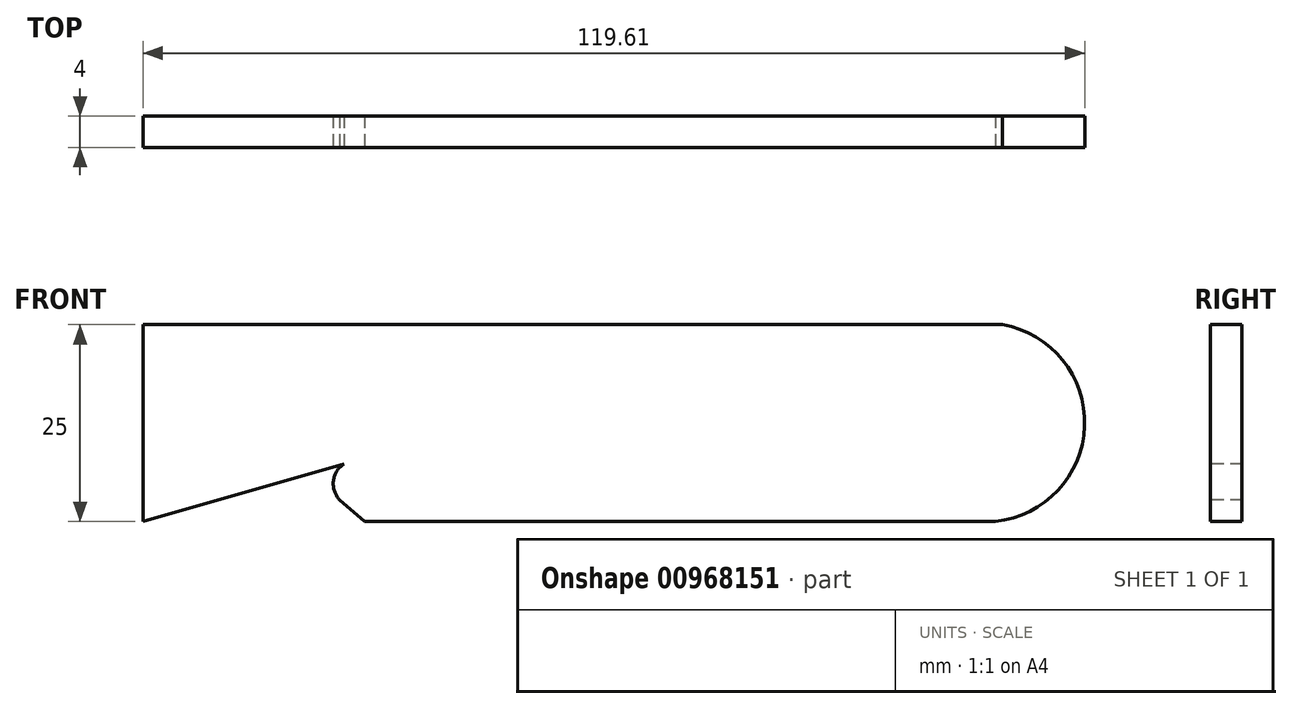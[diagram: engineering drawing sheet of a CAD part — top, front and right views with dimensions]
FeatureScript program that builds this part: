
annotation { "Feature Type Name" : "Feature", "Feature Type Description" : "" }
export const myFeature = defineFeature(function(context is Context, id is Id, definition is map)
    precondition{}
    {
        {
            var Q0;
            Q0=qCreatedBy(makeId("Front.planeOp"),FACE);
            var sketch = newSketch(context, id + "F0", { "sketchPlane" : qUnion([Q0])});
            skLineSegment(sketch, "E0.bottom", {"start": v(-16.89, -4.8) * mm, "end": v(103.11, -4.8) * mm});
            skLineSegment(sketch, "E0.top", {"start": v(-16.89, 20.2) * mm, "end": v(103.11, 20.2) * mm});
            skLineSegment(sketch, "E0.left", {"start": v(-16.89, -4.8) * mm, "end": v(-16.89, 20.2) * mm});
            skLineSegment(sketch, "E0.right", {"start": v(103.11, -4.8) * mm, "end": v(103.11, 20.2) * mm});
            skSolve(sketch);
        }
        {
            var Q0;
            Q0=makeQuery(id+"F0.imprint","IMPRINT",FACE,{"disambiguationData":[TD([[makeQuery(id+"F0.imprint","IMPRINT",EDGE,{"derivedFrom":sQuery(id+"F0.wireOp",EDGE,"E0.bottom")}),1.0]])]});
            extrude(context, id + "F1", {"entities" : qUnion([Q0]), "depth" : 4 * mm, "offsetDistance" : 25 * mm});
        }
        {
            var Q0;
            Q0=makeQuery(id+"F1.opExtrude","CAP_FACE",FACE,{"disambiguationData":[OSD([sQuery(id+"F0.wireOp",EDGE,"E0.bottom"),sQuery(id+"F0.wireOp",EDGE,"E0.top"),sQuery(id+"F0.wireOp",EDGE,"E0.left"),sQuery(id+"F0.wireOp",EDGE,"E0.right")])],"isStart":false});
            var sketch = newSketch(context, id + "F2", { "sketchPlane" : qUnion([Q0])});
            skArc(sketch, "E1", {"start": v(88.8, -4.8) * mm, "mid": v(102.72, 8.2) * mm, "end": v(87.92, 20.2) * mm});
            skSolve(sketch);
        }
        {
            var Q0;
            {var subQ5=makeQuery(id+"F1.opExtrude","CAP_EDGE",EDGE,{"disambiguationData":[OSD([sQuery(id+"F0.wireOp",EDGE,"E0.right")])],"isStart":false});Q0=makeQuery(id+"F2.imprint","IMPRINT",FACE,{"disambiguationData":[TD([[makeQuery(id+"F2.imprint","IMPRINT",EDGE,{"derivedFrom":subQ5}),1.0]])]});}
            extrude(context, id + "F3", {"entities" : qUnion([Q0]), "operationType" : NewBodyOperationType.REMOVE, "endBound" : BoundingType.THROUGH_ALL, "oppositeDirection" : true, "depth" : 25 * mm, "offsetDistance" : 25 * mm});
        }
        {
            var Q0;
            Q0=makeQuery(id+"F1.opExtrude","CAP_FACE",FACE,{"disambiguationData":[OSD([sQuery(id+"F0.wireOp",EDGE,"E0.bottom"),sQuery(id+"F0.wireOp",EDGE,"E0.top"),sQuery(id+"F0.wireOp",EDGE,"E0.left"),sQuery(id+"F0.wireOp",EDGE,"E0.right")])],"isStart":false});
            var sketch = newSketch(context, id + "F4", { "sketchPlane" : qUnion([Q0])});
            skCircle(sketch, "E2", {"center": v(10.27, 0) * mm, "radius": 3 * mm});
            skLineSegment(sketch, "E3", {"start": v(10.34, 3) * mm, "end": v(-16.89, -4.8) * mm});
            skLineSegment(sketch, "E4", {"start": v(8.08, -2.05) * mm, "end": v(11.22, -4.8) * mm});
            skSolve(sketch);
        }
        {
            var Q0;
            {var subQ0=sQuery(id+"F4.wireOp",EDGE,"E4");var subQ1=sQuery(id+"F4.wireOp",EDGE,"E2");var subQ2=makeQuery(id+"F4.imprint","INTERSECT",VERTEX,{"disambiguationData":[OD(0.0)],"derivedFrom":[subQ1,subQ0]});Q0=makeQuery(id+"F4.imprint","IMPRINT",FACE,{"disambiguationData":[TD([[makeQuery(id+"F4.imprint","IMPRINT",EDGE,{"disambiguationData":[TD([[subQ2,1.0]])],"derivedFrom":subQ1}),1.0]])]});}
            var Q1;
            {var subQ3=sQuery(id+"F4.wireOp",EDGE,"E2");var subQ5=sQuery(id+"F4.wireOp",EDGE,"E4");var subQ8=makeQuery(id+"F4.imprint","INTERSECT",VERTEX,{"disambiguationData":[OD(0.0)],"derivedFrom":[subQ3,subQ5]});Q1=makeQuery(id+"F4.imprint","IMPRINT",FACE,{"disambiguationData":[TD([[makeQuery(id+"F4.imprint","IMPRINT",EDGE,{"disambiguationData":[TD([[subQ8,1.0]])],"derivedFrom":subQ3}),-1.0]])]});}
            extrude(context, id + "F5", {"entities" : qUnion([Q0, Q1]), "operationType" : NewBodyOperationType.REMOVE, "endBound" : BoundingType.THROUGH_ALL, "oppositeDirection" : true, "depth" : 25 * mm, "offsetDistance" : 25 * mm});
        }
    });
